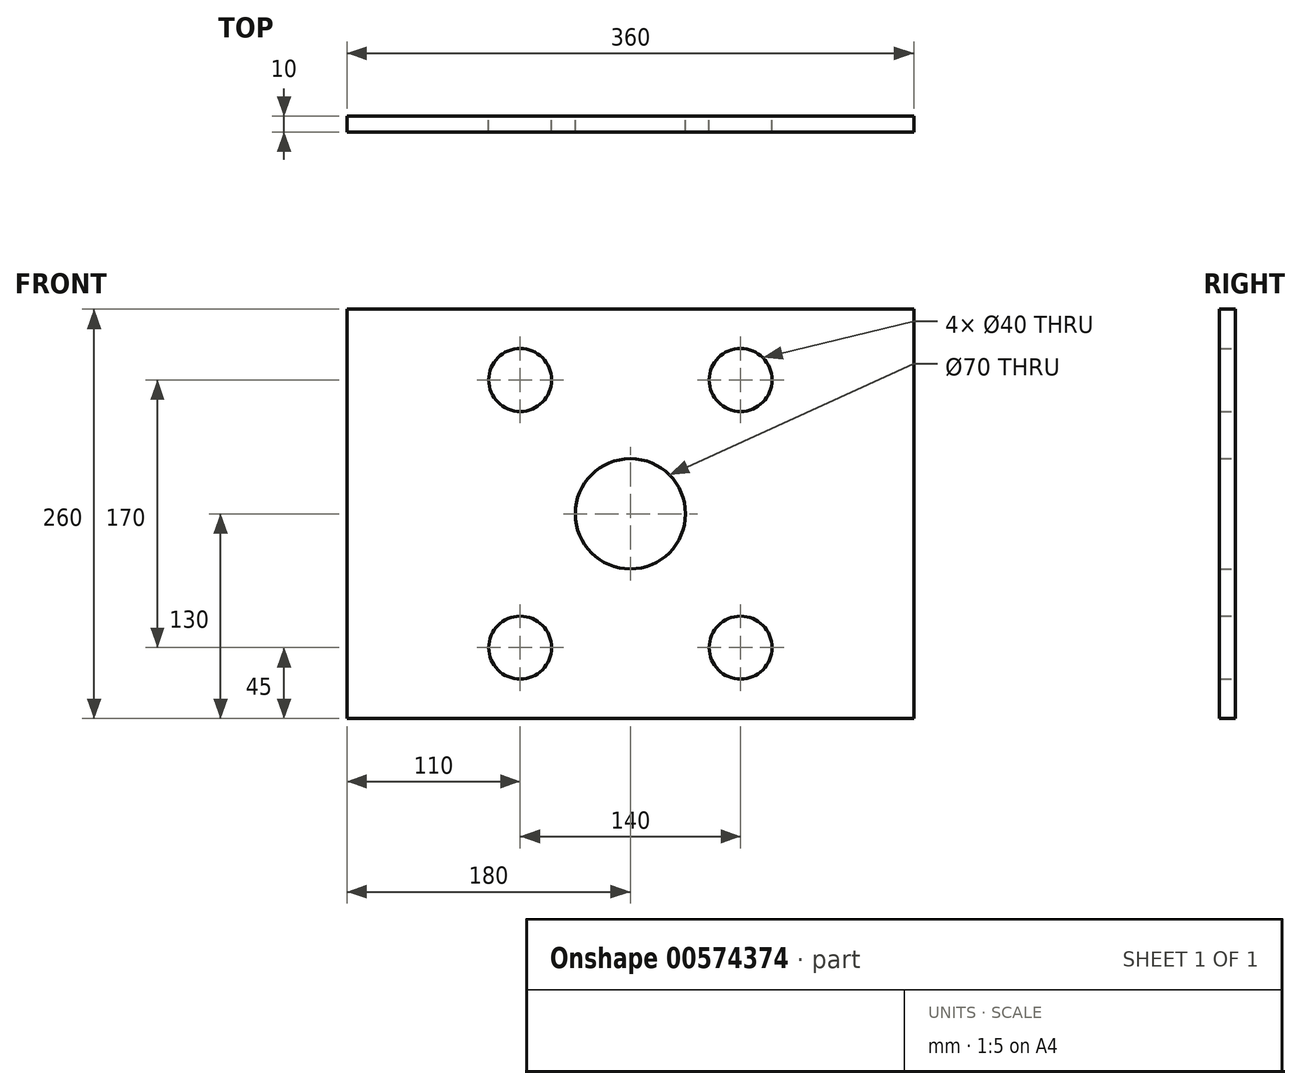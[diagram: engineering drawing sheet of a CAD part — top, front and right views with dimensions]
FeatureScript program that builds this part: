
annotation { "Feature Type Name" : "Feature", "Feature Type Description" : "" }
export const myFeature = defineFeature(function(context is Context, id is Id, definition is map)
    precondition{}
    {
        {
            var Q0;
            Q0=qCreatedBy(makeId("Front.planeOp"),FACE);
            var sketch = newSketch(context, id + "F0", { "sketchPlane" : qUnion([Q0])});
            skLineSegment(sketch, "E0.bottom", {"start": v(-180, 130) * mm, "end": v(180, 130) * mm});
            skLineSegment(sketch, "E0.top", {"start": v(-180, -130) * mm, "end": v(180, -130) * mm});
            skLineSegment(sketch, "E0.left", {"start": v(-180, 130) * mm, "end": v(-180, -130) * mm});
            skLineSegment(sketch, "E0.right", {"start": v(180, 130) * mm, "end": v(180, -130) * mm});
            skCircle(sketch, "E1", {"center": v(0, 0) * mm, "radius": 35 * mm});
            skLineSegment(sketch, "E2", {"start": v(-180, 85) * mm, "end": v(180, 85) * mm, "construction": true});
            skLineSegment(sketch, "E3", {"start": v(-180, -85) * mm, "end": v(180, -85) * mm, "construction": true});
            skCircle(sketch, "E4", {"center": v(-70, 85) * mm, "radius": 20 * mm});
            skCircle(sketch, "E5", {"center": v(70, 85) * mm, "radius": 20 * mm});
            skCircle(sketch, "E6", {"center": v(-70, -85) * mm, "radius": 20 * mm});
            skCircle(sketch, "E7", {"center": v(70, -85) * mm, "radius": 20 * mm});
            skSolve(sketch);
        }
        {
            var Q0;
            Q0=makeQuery(id+"F0.imprint","IMPRINT",FACE,{"disambiguationData":[TD([[makeQuery(id+"F0.imprint","IMPRINT",EDGE,{"derivedFrom":sQuery(id+"F0.wireOp",EDGE,"E0.bottom")}),-1.0]])]});
            extrude(context, id + "F1", {"entities" : qUnion([Q0]), "depth" : 10 * mm, "offsetDistance" : 25 * mm});
        }
    });
